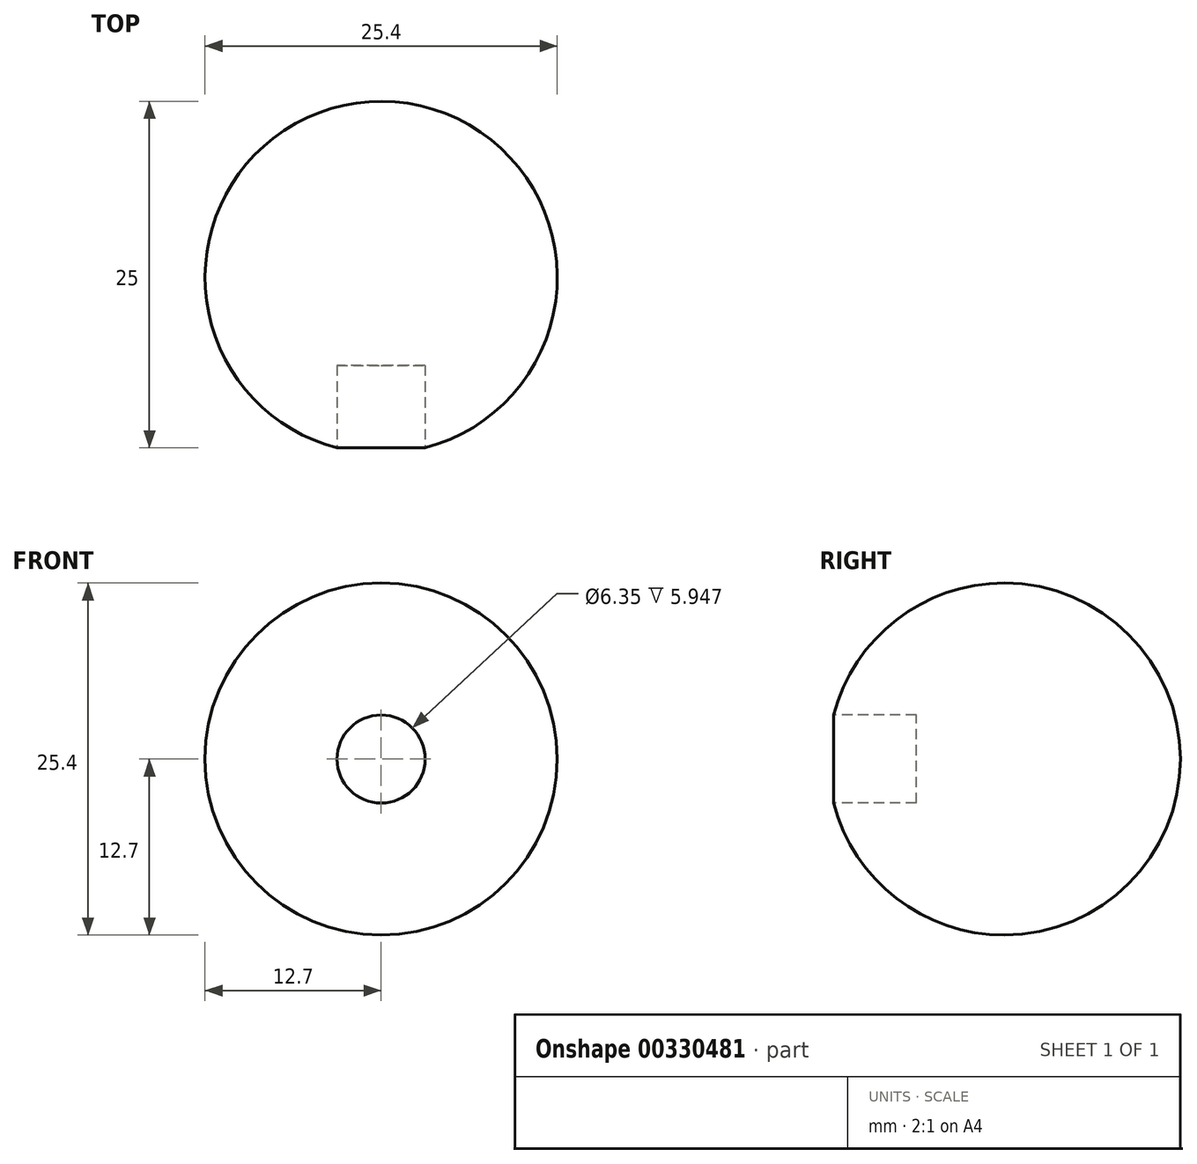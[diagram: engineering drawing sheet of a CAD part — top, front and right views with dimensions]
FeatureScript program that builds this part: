
annotation { "Feature Type Name" : "Feature", "Feature Type Description" : "" }
export const myFeature = defineFeature(function(context is Context, id is Id, definition is map)
    precondition{}
    {
        {
            var Q0;
            Q0=qCreatedBy(makeId("Front.planeOp"),FACE);
            var sketch = newSketch(context, id + "F0", { "sketchPlane" : qUnion([Q0])});
            skArc(sketch, "E0", {"start": v(0, 12.7) * mm, "mid": v(-12.7, 0) * mm, "end": v(0, -12.7) * mm});
            skLineSegment(sketch, "E1", {"start": v(0, 12.7) * mm, "end": v(0, -12.7) * mm});
            skSolve(sketch);
        }
        {
            var Q0;
            Q0=qCreatedBy(makeId("Top.planeOp"),FACE);
            var sketch = newSketch(context, id + "F1", { "sketchPlane" : qUnion([Q0])});
            skCircle(sketch, "E2", {"center": v(0, 0) * mm, "radius": 12.7 * mm});
            skSolve(sketch);
        }
        {
            var Q0;
            Q0=makeQuery(id+"F0.imprint","IMPRINT",FACE,{"disambiguationData":[TD([[makeQuery(id+"F0.imprint","IMPRINT",EDGE,{"derivedFrom":sQuery(id+"F0.wireOp",EDGE,"E0")}),1.0]])]});
            var Q1;
            Q1=sQuery(id+"F1.wireOp",EDGE,"E2");
            revolve(context, id + "F2", {"entities" : qUnion([Q0]), "axis" : qUnion([Q1]), "revolveType" : RevolveType.FULL});
        }
        {
            var Q0;
            Q0=qCreatedBy(makeId("Front.planeOp"),FACE);
            cPlane(context, id + "F3", {"entities" : qUnion([Q0]), "cplaneType" : CPlaneType.OFFSET, "offset" : 12.7 * mm, "width" : 152.4 * mm, "height" : 152.4 * mm});
        }
        {
            var Q0;
            Q0=qCreatedBy(id+"F3.planeOp",FACE);
            var sketch = newSketch(context, id + "F4", { "sketchPlane" : qUnion([Q0])});
            skCircle(sketch, "E3", {"center": v(0, 0) * mm, "radius": 3.18 * mm});
            skSolve(sketch);
        }
        {
            var Q0;
            Q0=qSketchRegion(id+"F4",true);
            extrude(context, id + "F5", {"entities" : qUnion([Q0]), "operationType" : NewBodyOperationType.REMOVE, "oppositeDirection" : true, "depth" : 6.35 * mm});
        }
        {
            var Q0;
            Q0=qCreatedBy(makeId("Front.planeOp"),FACE);
            cPlane(context, id + "F6", {"entities" : qUnion([Q0]), "cplaneType" : CPlaneType.OFFSET, "offset" : 12.7 * mm, "oppositeDirection" : true, "width" : 152.4 * mm, "height" : 152.4 * mm});
        }
        {
            var Q0;
            Q0=qCreatedBy(id+"F6.planeOp",FACE);
            var sketch = newSketch(context, id + "F7", { "sketchPlane" : qUnion([Q0])});
            skCircle(sketch, "E4", {"center": v(0, 0) * mm, "radius": 3.18 * mm});
            skSolve(sketch);
        }
        {
            var Q0;
            Q0=makeQuery(id+"F7.imprint","IMPRINT",FACE,{"disambiguationData":[TD([[makeQuery(id+"F7.imprint","IMPRINT",EDGE,{"derivedFrom":sQuery(id+"F7.wireOp",EDGE,"E4")}),1.0]])]});
            extrude(context, id + "F8", {"entities" : qUnion([Q0]), "depth" : 9.52 * mm});
        }
        {
            var Q0;
            Q0=makeQuery(id+"F8.opExtrude","SWEPT_BODY",BODY,{"disambiguationData":[OSD([sQuery(id+"F7.wireOp",EDGE,"E4")])]});
            deleteBodies(context, id + "F9", {"entities" : qUnion([Q0])});
        }
    });
